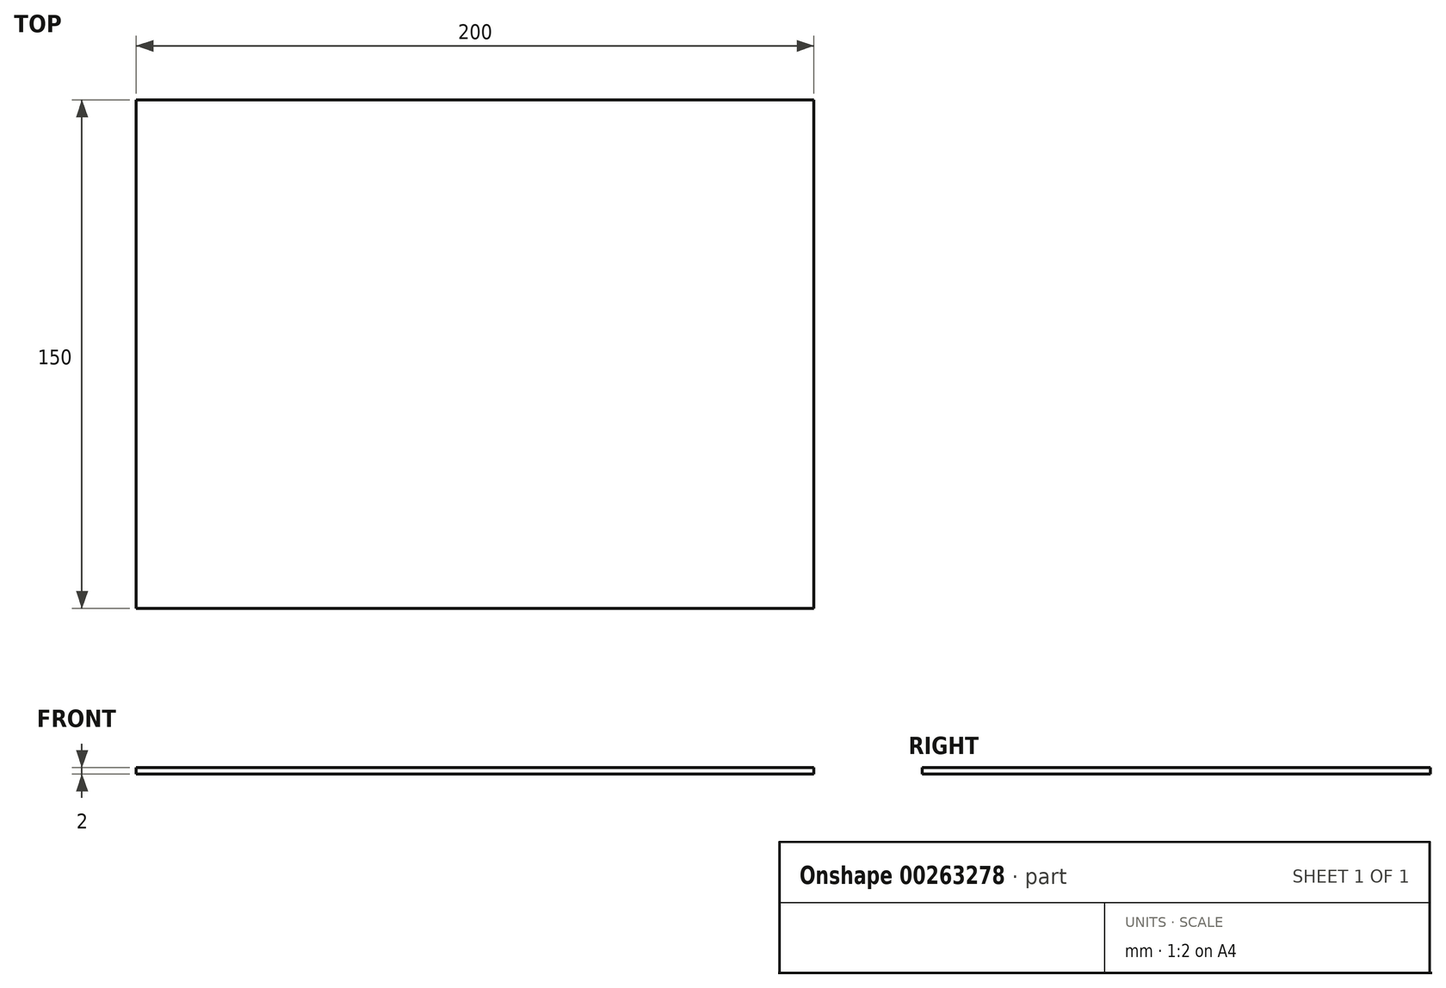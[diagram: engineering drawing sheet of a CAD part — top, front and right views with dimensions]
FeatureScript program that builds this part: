
annotation { "Feature Type Name" : "Feature", "Feature Type Description" : "" }
export const myFeature = defineFeature(function(context is Context, id is Id, definition is map)
    precondition{}
    {
        {
            var Q0;
            Q0=qCreatedBy(makeId("Top.planeOp"),FACE);
            var sketch = newSketch(context, id + "F0", { "sketchPlane" : qUnion([Q0])});
            skLineSegment(sketch, "E0.bottom", {"start": v(100, -75) * mm, "end": v(-100, -75) * mm});
            skLineSegment(sketch, "E0.top", {"start": v(100, 75) * mm, "end": v(-100, 75) * mm});
            skLineSegment(sketch, "E0.left", {"start": v(100, -75) * mm, "end": v(100, 75) * mm});
            skLineSegment(sketch, "E0.right", {"start": v(-100, -75) * mm, "end": v(-100, 75) * mm});
            skPoint(sketch, "E0.middle", {"position": v(0, 0) * mm});
            skSolve(sketch);
        }
        {
            var Q0;
            Q0 = qSketchRegion(id + "F0", true);
            extrude(context, id + "F1", {"entities" : qUnion([Q0]), "depth" : 2 * mm});
        }
    });
